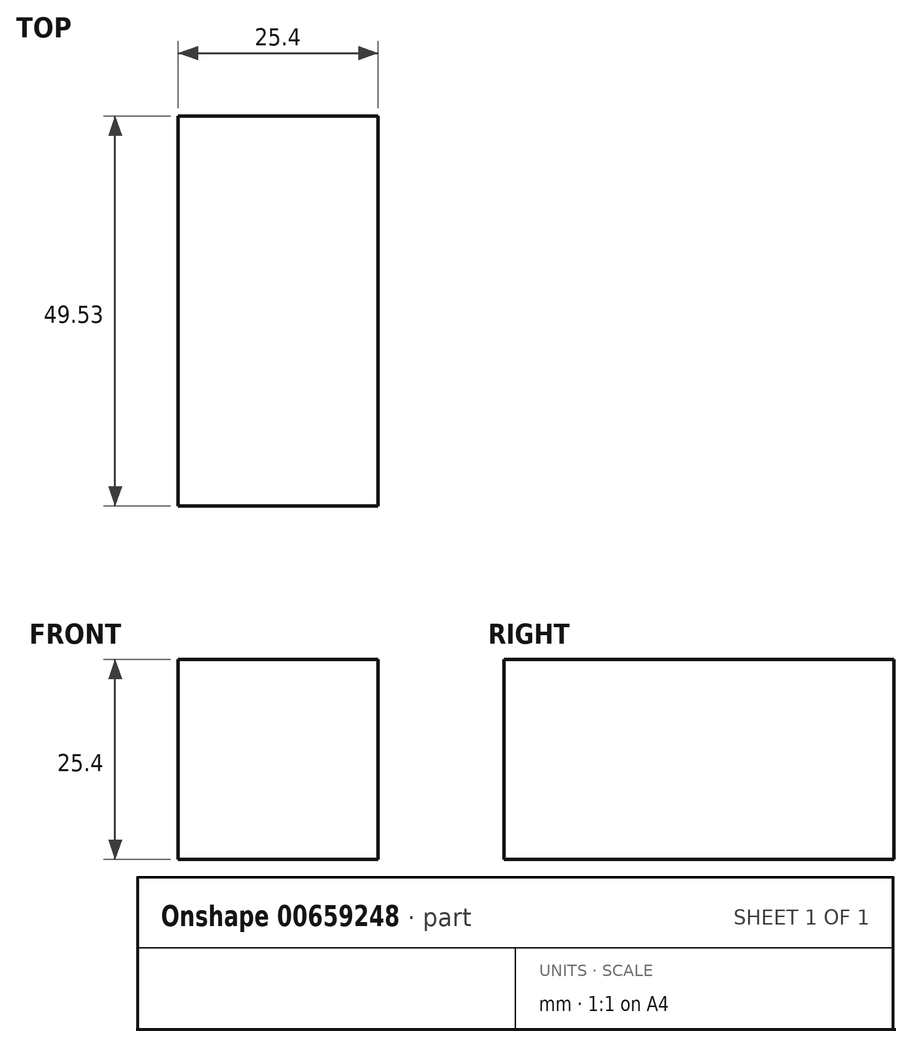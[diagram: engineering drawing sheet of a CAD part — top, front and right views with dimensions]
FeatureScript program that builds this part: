
annotation { "Feature Type Name" : "Feature", "Feature Type Description" : "" }
export const myFeature = defineFeature(function(context is Context, id is Id, definition is map)
    precondition{}
    {
        {
            var Q0;
            Q0=qCreatedBy(makeId("Front.planeOp"),FACE);
            var sketch = newSketch(context, id + "F0", { "sketchPlane" : qUnion([Q0])});
            skLineSegment(sketch, "E0.bottom", {"start": v(12.7, 12.7) * mm, "end": v(-12.7, 12.7) * mm});
            skLineSegment(sketch, "E0.top", {"start": v(12.7, -12.7) * mm, "end": v(-12.7, -12.7) * mm});
            skLineSegment(sketch, "E0.left", {"start": v(12.7, 12.7) * mm, "end": v(12.7, -12.7) * mm});
            skLineSegment(sketch, "E0.right", {"start": v(-12.7, 12.7) * mm, "end": v(-12.7, -12.7) * mm});
            skPoint(sketch, "E0.middle", {"position": v(0, 0) * mm});
            skSolve(sketch);
        }
        {
            var Q0;
            Q0=makeQuery(id+"F0.imprint","IMPRINT",FACE,{"disambiguationData":[TD([[makeQuery(id+"F0.imprint","IMPRINT",EDGE,{"derivedFrom":sQuery(id+"F0.wireOp",EDGE,"E0.bottom")}),1.0]])]});
            extrude(context, id + "F1", {"entities" : qUnion([Q0]), "depth" : 49.53 * mm, "offsetDistance" : 25.4 * mm});
        }
    });
